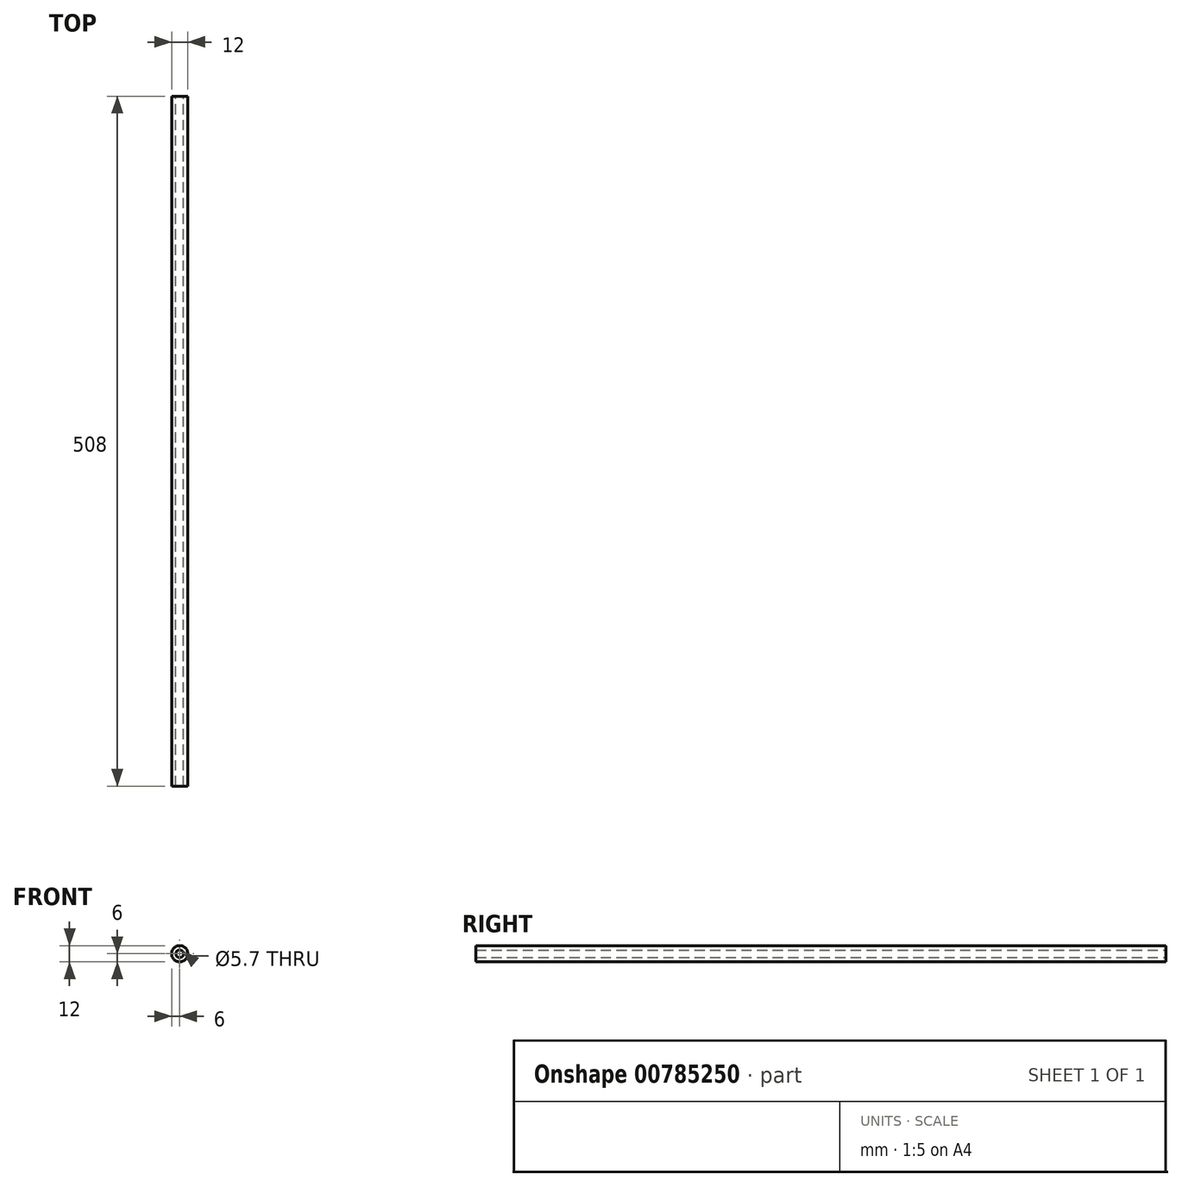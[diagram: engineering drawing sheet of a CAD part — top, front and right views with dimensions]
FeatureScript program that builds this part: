
annotation { "Feature Type Name" : "Feature", "Feature Type Description" : "" }
export const myFeature = defineFeature(function(context is Context, id is Id, definition is map)
    precondition{}
    {
        {
            var Q0;
            Q0=qCreatedBy(makeId("Front.planeOp"),FACE);
            var sketch = newSketch(context, id + "F0", { "sketchPlane" : qUnion([Q0])});
            skCircle(sketch, "E0", {"center": v(0, 0) * mm, "radius": 2.85 * mm});
            skCircle(sketch, "E1", {"center": v(0, 0) * mm, "radius": 6 * mm});
            skSolve(sketch);
        }
        {
            var Q0;
            Q0=makeQuery(id+"F0.imprint","IMPRINT",FACE,{"disambiguationData":[TD([[makeQuery(id+"F0.imprint","IMPRINT",EDGE,{"derivedFrom":sQuery(id+"F0.wireOp",EDGE,"E0")}),-1.0]])]});
            extrude(context, id + "F1", {"entities" : qUnion([Q0]), "depth" : 508 * mm, "offsetDistance" : 25 * mm});
        }
    });
